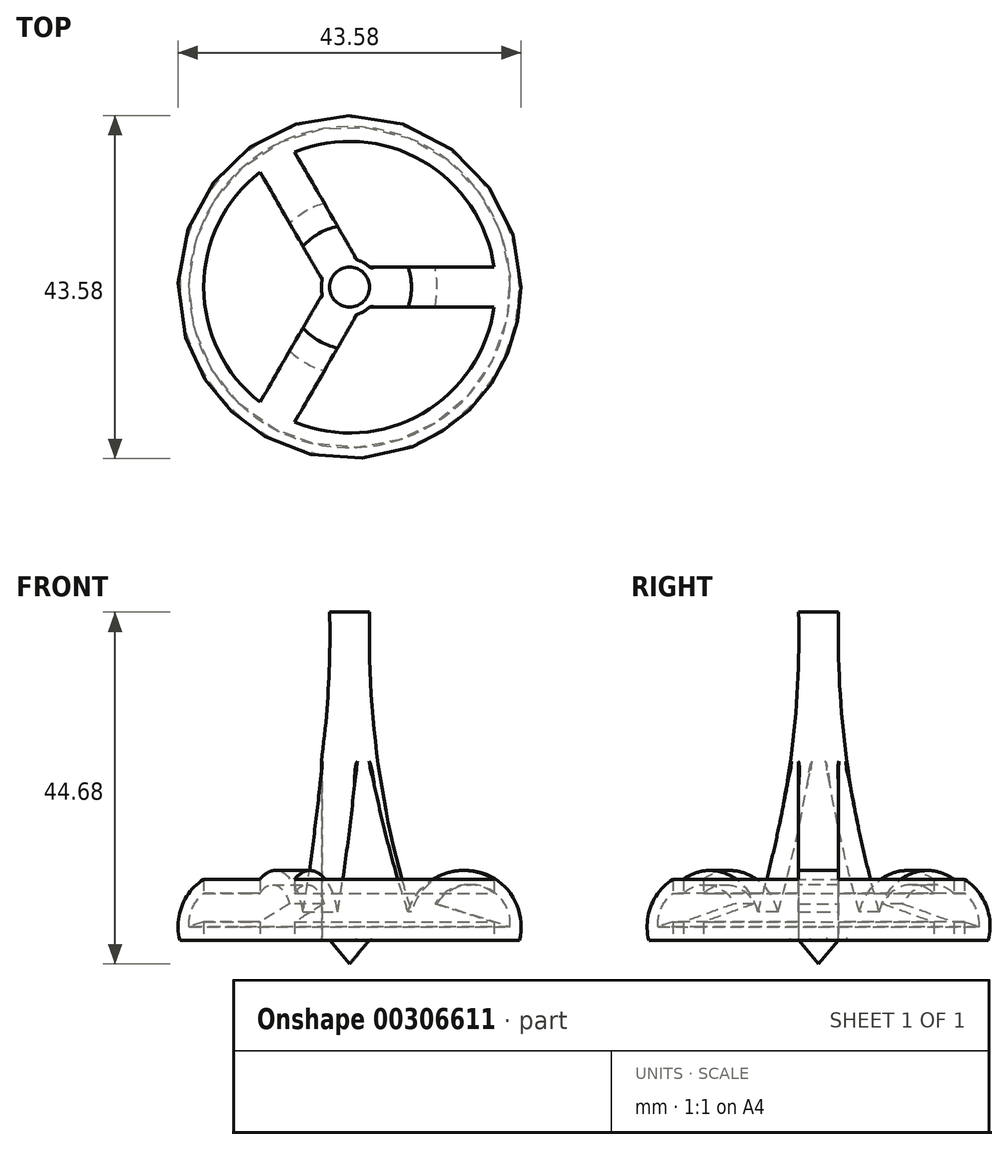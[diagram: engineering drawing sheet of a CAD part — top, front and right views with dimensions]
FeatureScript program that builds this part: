
annotation { "Feature Type Name" : "Feature", "Feature Type Description" : "" }
export const myFeature = defineFeature(function(context is Context, id is Id, definition is map)
    precondition{}
    {
        {
            var Q0;
            Q0=qCreatedBy(makeId("Front.planeOp"),FACE);
            var sketch = newSketch(context, id + "F0", { "sketchPlane" : qUnion([Q0])});
            skArc(sketch, "E0", {"start": v(0, 0) * mm, "mid": v(1.1, -19.27) * mm, "end": v(5.32, -38.1) * mm});
            skLineSegment(sketch, "E1", {"start": v(0, 0) * mm, "end": v(-2.54, 0) * mm});
            skLineSegment(sketch, "E2", {"start": v(-2.54, 0) * mm, "end": v(-2.54, -44.68) * mm});
            skLineSegment(sketch, "E3", {"start": v(-2.54, -44.68) * mm, "end": v(-0.03, -41.68) * mm});
            skLineSegment(sketch, "E4", {"start": v(-0.03, -41.68) * mm, "end": v(19.02, -41.68) * mm});
            skArc(sketch, "E5", {"start": v(19.02, -41.68) * mm, "mid": v(13.96, -33.04) * mm, "end": v(5.32, -38.1) * mm});
            skSolve(sketch);
        }
        {
            var Q0;
            Q0 = qSketchRegion(id + "F0", true);
            var Q1;
            Q1=sQuery(id+"F0.wireOp",EDGE,"E2");
            revolve(context, id + "F1", {"entities" : qUnion([Q0]), "axis" : qUnion([Q1]), "revolveType" : RevolveType.FULL});
        }
        {
            var Q0;
            Q0=makeQuery(id+"F1.opRevolve","SWEPT_FACE",FACE,{"disambiguationData":[OSD([sQuery(id+"F0.wireOp",EDGE,"E4")])]});
            var sketch = newSketch(context, id + "F2", { "sketchPlane" : qUnion([Q0])});
            skLineSegment(sketch, "E6.0", {"start": v(0, -2.54) * mm, "end": v(15.8, -2.54) * mm});
            skLineSegment(sketch, "E7.0", {"start": v(0, 2.54) * mm, "end": v(15.8, 2.54) * mm});
            skArc(sketch, "E8", {"start": v(-6, 0.93) * mm, "mid": v(-6.13, 0) * mm, "end": v(-6, -0.93) * mm});
            skArc(sketch, "E9", {"start": v(-13.91, 14.62) * mm, "mid": v(-21.06, 0) * mm, "end": v(-13.91, -14.62) * mm, "construction": true});
            skLineSegment(sketch, "E10.1.0", {"start": v(-6, 0.93) * mm, "end": v(-13.91, 14.62) * mm});
            skLineSegment(sketch, "E10.1.1", {"start": v(-1.61, 3.47) * mm, "end": v(-9.51, 17.16) * mm});
            skLineSegment(sketch, "E10.2.0", {"start": v(-1.61, -3.47) * mm, "end": v(-9.51, -17.16) * mm});
            skLineSegment(sketch, "E10.2.1", {"start": v(-6, -0.93) * mm, "end": v(-13.91, -14.62) * mm});
            skArc(sketch, "E11", {"start": v(-13.91, 14.62) * mm, "mid": v(-21.06, 0) * mm, "end": v(-13.91, -14.62) * mm});
            skArc(sketch, "E12.trimOffspring", {"start": v(0, 2.54) * mm, "mid": v(-0.74, 3.11) * mm, "end": v(-1.61, 3.47) * mm});
            skArc(sketch, "E13.trimOffspring", {"start": v(-1.61, -3.47) * mm, "mid": v(-0.74, -3.11) * mm, "end": v(0, -2.54) * mm});
            skArc(sketch, "E14.trimOffspring", {"start": v(15.8, 2.54) * mm, "mid": v(6.72, 16.04) * mm, "end": v(-9.51, 17.16) * mm, "construction": true});
            skArc(sketch, "E15.trimOffspring", {"start": v(-9.51, -17.16) * mm, "mid": v(6.72, -16.04) * mm, "end": v(15.8, -2.54) * mm, "construction": true});
            skArc(sketch, "E16.trimOffspring", {"start": v(-9.51, -17.16) * mm, "mid": v(6.72, -16.04) * mm, "end": v(15.8, -2.54) * mm});
            skArc(sketch, "E17.trimOffspring", {"start": v(15.8, 2.54) * mm, "mid": v(6.72, 16.04) * mm, "end": v(-9.51, 17.16) * mm});
            skSolve(sketch);
        }
        {
            var Q0;
            Q0 = qSketchRegion(id + "F2", true);
            extrude(context, id + "F3", {"entities" : qUnion([Q0]), "operationType" : NewBodyOperationType.REMOVE, "oppositeDirection" : true, "depth" : 25.4 * mm});
        }
        {
            var Q0;
            Q0=makeQuery(id+"F3.boolean.opBoolean","COPY",FACE,{"derivedFrom":makeQuery(id+"F3.opExtrude","SWEPT_FACE",FACE,{"disambiguationData":[OSD([sQuery(id+"F2.wireOp",EDGE,"E13.trimOffspring")])]})});
            var Q1;
            Q1=makeQuery(id+"F3.boolean.opBoolean","COPY",FACE,{"derivedFrom":makeQuery(id+"F3.opExtrude","SWEPT_FACE",FACE,{"disambiguationData":[OSD([sQuery(id+"F2.wireOp",EDGE,"E8")])]})});
            var Q2;
            Q2=makeQuery(id+"F3.boolean.opBoolean","COPY",FACE,{"derivedFrom":makeQuery(id+"F3.opExtrude","SWEPT_FACE",FACE,{"disambiguationData":[OSD([sQuery(id+"F2.wireOp",EDGE,"E12.trimOffspring")])]})});
            fillet(context, id + "F4", {"entities" : qUnion([Q0, Q1, Q2]), "radius" : 0.25 * mm, "tangentPropagation" : true, "allowEdgeOverflow" : false});
        }
        {
            var Q0;
            Q0=makeQuery(id+"F3.boolean.opBoolean","COPY",FACE,{"derivedFrom":makeQuery(id+"F3.opExtrude","SWEPT_FACE",FACE,{"disambiguationData":[OSD([sQuery(id+"F2.wireOp",EDGE,"E7.0")])]})});
            var Q1;
            Q1=makeQuery(id+"F3.boolean.opBoolean","COPY",FACE,{"derivedFrom":makeQuery(id+"F3.opExtrude","SWEPT_FACE",FACE,{"disambiguationData":[OSD([sQuery(id+"F2.wireOp",EDGE,"E6.0")])]})});
            cPlane(context, id + "F5", {"entities" : qUnion([Q0, Q1]), "cplaneType" : CPlaneType.MID_PLANE, "offset" : 25.4 * mm, "width" : 152.4 * mm, "height" : 152.4 * mm});
        }
        {
            var Q0;
            Q0=qCreatedBy(id+"F5.planeOp",FACE);
            var sketch = newSketch(context, id + "F6", { "sketchPlane" : qUnion([Q0])});
            skLineSegment(sketch, "E18", {"start": v(-2.54, -44.68) * mm, "end": v(-2.54, -1.8) * mm});
            skArc(sketch, "E19", {"start": v(17.85, -39.95) * mm, "mid": v(14.37, -34.84) * mm, "end": v(8.58, -37.03) * mm});
            skLineSegment(sketch, "E20", {"start": v(8.58, -37.03) * mm, "end": v(17.85, -39.95) * mm});
            skSolve(sketch);
        }
        {
            var Q0;
            Q0 = qSketchRegion(id + "F6", true);
            var Q1;
            Q1=sQuery(id+"F6.wireOp",EDGE,"E18");
            revolve(context, id + "F7", {"operationType" : NewBodyOperationType.REMOVE, "entities" : qUnion([Q0]), "axis" : qUnion([Q1]), "revolveType" : RevolveType.FULL, "oppositeDirection" : true});
        }
    });
